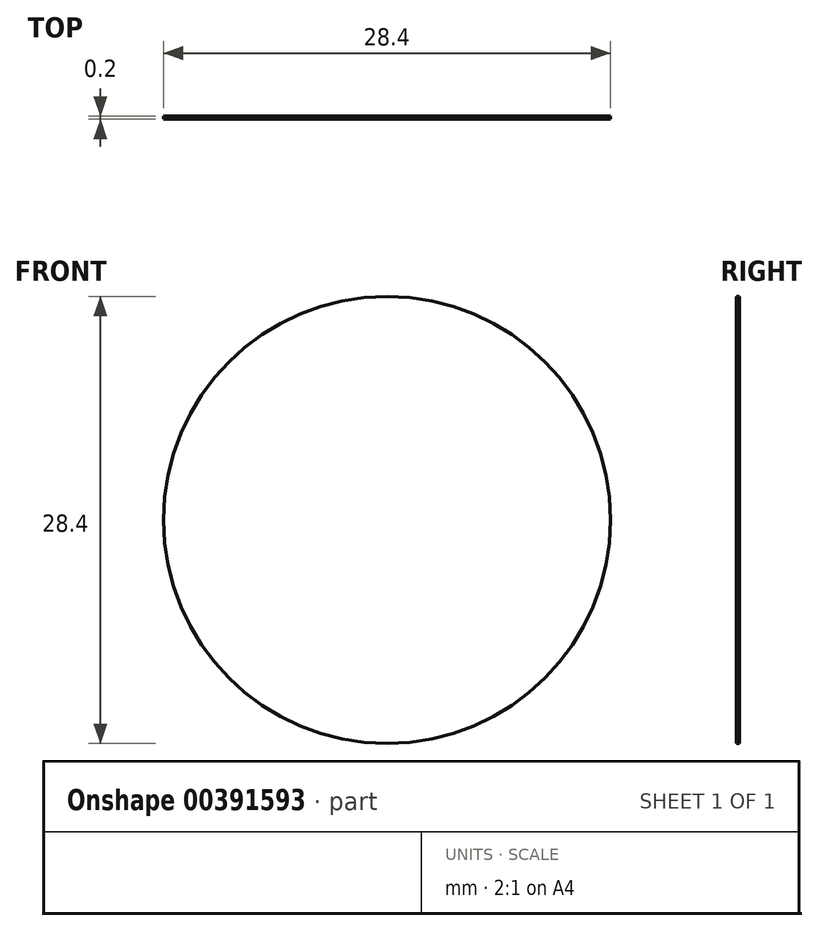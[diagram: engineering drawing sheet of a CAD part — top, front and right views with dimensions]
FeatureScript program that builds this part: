
annotation { "Feature Type Name" : "Feature", "Feature Type Description" : "" }
export const myFeature = defineFeature(function(context is Context, id is Id, definition is map)
    precondition{}
    {
        {
            var Q0;
            Q0=qCreatedBy(makeId("Front.planeOp"),FACE);
            var sketch = newSketch(context, id + "F0", { "sketchPlane" : qUnion([Q0])});
            skCircle(sketch, "E0", {"center": v(0, 0) * mm, "radius": 7 * mm, "construction": true});
            skCircle(sketch, "E1", {"center": v(0, 0) * mm, "radius": 10.5 * mm, "construction": true});
            skLineSegment(sketch, "E2", {"start": v(0, 7) * mm, "end": v(0.75, 7) * mm, "construction": true});
            skLineSegment(sketch, "E3", {"start": v(0.75, 7) * mm, "end": v(0.75, 13.5) * mm, "construction": true});
            skLineSegment(sketch, "E4", {"start": v(0.75, 13.5) * mm, "end": v(0, 13.5) * mm, "construction": true});
            skLineSegment(sketch, "E5", {"start": v(0, 13.5) * mm, "end": v(-0.75, 13.5) * mm, "construction": true});
            skLineSegment(sketch, "E6", {"start": v(-0.75, 13.5) * mm, "end": v(-0.75, 7) * mm, "construction": true});
            skLineSegment(sketch, "E7", {"start": v(-0.75, 7) * mm, "end": v(0, 7) * mm, "construction": true});
            skLineSegment(sketch, "E8.1.0", {"start": v(-2.85, 6.44) * mm, "end": v(-6.1, 12.07) * mm});
            skLineSegment(sketch, "E8.1.1", {"start": v(-7.4, 11.32) * mm, "end": v(-4.15, 5.69) * mm});
            skLineSegment(sketch, "E8.1.2", {"start": v(-4.15, 5.69) * mm, "end": v(-3.5, 6.06) * mm});
            skLineSegment(sketch, "E8.1.3", {"start": v(-3.5, 6.06) * mm, "end": v(-2.85, 6.44) * mm});
            skLineSegment(sketch, "E8.1.4", {"start": v(-6.1, 12.07) * mm, "end": v(-6.75, 11.7) * mm});
            skLineSegment(sketch, "E8.1.5", {"start": v(-6.75, 11.7) * mm, "end": v(-7.4, 11.32) * mm});
            skLineSegment(sketch, "E8.2.0", {"start": v(-5.69, 4.15) * mm, "end": v(-11.32, 7.4) * mm});
            skLineSegment(sketch, "E8.2.1", {"start": v(-12.07, 6.1) * mm, "end": v(-6.44, 2.85) * mm});
            skLineSegment(sketch, "E8.2.2", {"start": v(-6.44, 2.85) * mm, "end": v(-6.06, 3.5) * mm});
            skLineSegment(sketch, "E8.2.3", {"start": v(-6.06, 3.5) * mm, "end": v(-5.69, 4.15) * mm});
            skLineSegment(sketch, "E8.2.4", {"start": v(-11.32, 7.4) * mm, "end": v(-11.7, 6.75) * mm});
            skLineSegment(sketch, "E8.2.5", {"start": v(-11.7, 6.75) * mm, "end": v(-12.07, 6.1) * mm});
            skLineSegment(sketch, "E8.3.0", {"start": v(-7, 0.75) * mm, "end": v(-13.5, 0.75) * mm, "construction": true});
            skLineSegment(sketch, "E8.3.1", {"start": v(-13.5, -0.75) * mm, "end": v(-7, -0.75) * mm, "construction": true});
            skLineSegment(sketch, "E8.3.2", {"start": v(-7, -0.75) * mm, "end": v(-7, 0) * mm, "construction": true});
            skLineSegment(sketch, "E8.3.3", {"start": v(-7, 0) * mm, "end": v(-7, 0.75) * mm, "construction": true});
            skLineSegment(sketch, "E8.3.4", {"start": v(-13.5, 0.75) * mm, "end": v(-13.5, 0) * mm, "construction": true});
            skLineSegment(sketch, "E8.3.5", {"start": v(-13.5, 0) * mm, "end": v(-13.5, -0.75) * mm, "construction": true});
            skLineSegment(sketch, "E8.4.0", {"start": v(-6.44, -2.85) * mm, "end": v(-12.07, -6.1) * mm});
            skLineSegment(sketch, "E8.4.1", {"start": v(-11.32, -7.4) * mm, "end": v(-5.69, -4.15) * mm});
            skLineSegment(sketch, "E8.4.2", {"start": v(-5.69, -4.15) * mm, "end": v(-6.06, -3.5) * mm});
            skLineSegment(sketch, "E8.4.3", {"start": v(-6.06, -3.5) * mm, "end": v(-6.44, -2.85) * mm});
            skLineSegment(sketch, "E8.4.4", {"start": v(-12.07, -6.1) * mm, "end": v(-11.7, -6.75) * mm});
            skLineSegment(sketch, "E8.4.5", {"start": v(-11.7, -6.75) * mm, "end": v(-11.32, -7.4) * mm});
            skLineSegment(sketch, "E8.5.0", {"start": v(-4.15, -5.69) * mm, "end": v(-7.4, -11.32) * mm});
            skLineSegment(sketch, "E8.5.1", {"start": v(-6.1, -12.07) * mm, "end": v(-2.85, -6.44) * mm});
            skLineSegment(sketch, "E8.5.2", {"start": v(-2.85, -6.44) * mm, "end": v(-3.5, -6.06) * mm});
            skLineSegment(sketch, "E8.5.3", {"start": v(-3.5, -6.06) * mm, "end": v(-4.15, -5.69) * mm});
            skLineSegment(sketch, "E8.5.4", {"start": v(-7.4, -11.32) * mm, "end": v(-6.75, -11.7) * mm});
            skLineSegment(sketch, "E8.5.5", {"start": v(-6.75, -11.7) * mm, "end": v(-6.1, -12.07) * mm});
            skLineSegment(sketch, "E8.6.0", {"start": v(-0.75, -7) * mm, "end": v(-0.75, -13.5) * mm, "construction": true});
            skLineSegment(sketch, "E8.6.1", {"start": v(0.75, -13.5) * mm, "end": v(0.75, -7) * mm, "construction": true});
            skLineSegment(sketch, "E8.6.2", {"start": v(0.75, -7) * mm, "end": v(0, -7) * mm, "construction": true});
            skLineSegment(sketch, "E8.6.3", {"start": v(0, -7) * mm, "end": v(-0.75, -7) * mm, "construction": true});
            skLineSegment(sketch, "E8.6.4", {"start": v(-0.75, -13.5) * mm, "end": v(0, -13.5) * mm, "construction": true});
            skLineSegment(sketch, "E8.6.5", {"start": v(0, -13.5) * mm, "end": v(0.75, -13.5) * mm, "construction": true});
            skLineSegment(sketch, "E8.7.0", {"start": v(2.85, -6.44) * mm, "end": v(6.1, -12.07) * mm});
            skLineSegment(sketch, "E8.7.1", {"start": v(7.4, -11.32) * mm, "end": v(4.15, -5.69) * mm});
            skLineSegment(sketch, "E8.7.2", {"start": v(4.15, -5.69) * mm, "end": v(3.5, -6.06) * mm});
            skLineSegment(sketch, "E8.7.3", {"start": v(3.5, -6.06) * mm, "end": v(2.85, -6.44) * mm});
            skLineSegment(sketch, "E8.7.4", {"start": v(6.1, -12.07) * mm, "end": v(6.75, -11.7) * mm});
            skLineSegment(sketch, "E8.7.5", {"start": v(6.75, -11.7) * mm, "end": v(7.4, -11.32) * mm});
            skLineSegment(sketch, "E8.8.0", {"start": v(5.69, -4.15) * mm, "end": v(11.32, -7.4) * mm});
            skLineSegment(sketch, "E8.8.1", {"start": v(12.07, -6.1) * mm, "end": v(6.44, -2.85) * mm});
            skLineSegment(sketch, "E8.8.2", {"start": v(6.44, -2.85) * mm, "end": v(6.06, -3.5) * mm});
            skLineSegment(sketch, "E8.8.3", {"start": v(6.06, -3.5) * mm, "end": v(5.69, -4.15) * mm});
            skLineSegment(sketch, "E8.8.4", {"start": v(11.32, -7.4) * mm, "end": v(11.7, -6.75) * mm});
            skLineSegment(sketch, "E8.8.5", {"start": v(11.7, -6.75) * mm, "end": v(12.07, -6.1) * mm});
            skLineSegment(sketch, "E8.9.0", {"start": v(7, -0.75) * mm, "end": v(13.5, -0.75) * mm, "construction": true});
            skLineSegment(sketch, "E8.9.1", {"start": v(13.5, 0.75) * mm, "end": v(7, 0.75) * mm, "construction": true});
            skLineSegment(sketch, "E8.9.2", {"start": v(7, 0.75) * mm, "end": v(7, 0) * mm, "construction": true});
            skLineSegment(sketch, "E8.9.3", {"start": v(7, 0) * mm, "end": v(7, -0.75) * mm, "construction": true});
            skLineSegment(sketch, "E8.9.4", {"start": v(13.5, -0.75) * mm, "end": v(13.5, 0) * mm, "construction": true});
            skLineSegment(sketch, "E8.9.5", {"start": v(13.5, 0) * mm, "end": v(13.5, 0.75) * mm, "construction": true});
            skLineSegment(sketch, "E8.10.0", {"start": v(6.44, 2.85) * mm, "end": v(12.07, 6.1) * mm});
            skLineSegment(sketch, "E8.10.1", {"start": v(11.32, 7.4) * mm, "end": v(5.69, 4.15) * mm});
            skLineSegment(sketch, "E8.10.2", {"start": v(5.69, 4.15) * mm, "end": v(6.06, 3.5) * mm});
            skLineSegment(sketch, "E8.10.3", {"start": v(6.06, 3.5) * mm, "end": v(6.44, 2.85) * mm});
            skLineSegment(sketch, "E8.10.4", {"start": v(12.07, 6.1) * mm, "end": v(11.7, 6.75) * mm});
            skLineSegment(sketch, "E8.10.5", {"start": v(11.7, 6.75) * mm, "end": v(11.32, 7.4) * mm});
            skLineSegment(sketch, "E8.11.0", {"start": v(4.15, 5.69) * mm, "end": v(7.4, 11.32) * mm});
            skLineSegment(sketch, "E8.11.1", {"start": v(6.1, 12.07) * mm, "end": v(2.85, 6.44) * mm});
            skLineSegment(sketch, "E8.11.2", {"start": v(2.85, 6.44) * mm, "end": v(3.5, 6.06) * mm});
            skLineSegment(sketch, "E8.11.3", {"start": v(3.5, 6.06) * mm, "end": v(4.15, 5.69) * mm});
            skLineSegment(sketch, "E8.11.4", {"start": v(7.4, 11.32) * mm, "end": v(6.75, 11.7) * mm});
            skLineSegment(sketch, "E8.11.5", {"start": v(6.75, 11.7) * mm, "end": v(6.1, 12.07) * mm});
            skCircle(sketch, "E9", {"center": v(0, 0) * mm, "radius": 13.5 * mm, "construction": true});
            skSolve(sketch);
        }
        {
            var Q0;
            Q0=qCreatedBy(makeId("Front.planeOp"),FACE);
            var sketch = newSketch(context, id + "F1", { "sketchPlane" : qUnion([Q0])});
            skText(sketch, "E10", { "text": "12", "fontName": "AllertaStencil-Regular.ttf"});
            skText(sketch, "E11", { "text": "6", "fontName": "AllertaStencil-Regular.ttf"});
            skText(sketch, "E12", { "text": "9", "fontName": "AllertaStencil-Regular.ttf"});
            skPoint(sketch, "E13", {"position": v(-10.5, 0) * mm});
            skText(sketch, "E14", { "text": "3", "fontName": "AllertaStencil-Regular.ttf"});
            skCircle(sketch, "E15", {"center": v(0, 0) * mm, "radius": 10.5 * mm, "construction": true});
            skCircle(sketch, "E16", {"center": v(0, 0) * mm, "radius": 7 * mm, "construction": true});
            skLineSegment(sketch, "E17", {"start": v(0, 0) * mm, "end": v(0, 10.5) * mm, "construction": true});
            skLineSegment(sketch, "E18.1.0", {"start": v(0, 0) * mm, "end": v(-10.5, 0) * mm, "construction": true});
            skLineSegment(sketch, "E18.2.0", {"start": v(0, 0) * mm, "end": v(0, -10.5) * mm, "construction": true});
            skLineSegment(sketch, "E18.3.0", {"start": v(0, 0) * mm, "end": v(10.5, 0) * mm, "construction": true});
            skPoint(sketch, "E19", {"position": v(10.5, 0) * mm});
            const initialGuessF1  = {"E10": [-0.00246, 0.007, 1, 0, 0.0035], "E11": [-0.00153, -0.0105, 1, 0, 0.0035], "E12": [-0.0105, -0.00175, 1, 0, 0.0035], "E14": [0.00776, -0.00175, 1, 0, 0.0035]};
            skSetInitialGuess(sketch, initialGuessF1);
            skSolve(sketch);
        }
        {
            var Q0;
            Q0=qCreatedBy(makeId("Front.planeOp"),FACE);
            var sketch = newSketch(context, id + "F2", { "sketchPlane" : qUnion([Q0])});
            skLineSegment(sketch, "E20", {"start": v(0, 10.42) * mm, "end": v(1.75, 13.46) * mm});
            skLineSegment(sketch, "E21", {"start": v(1.75, 13.46) * mm, "end": v(-1.75, 13.46) * mm});
            skLineSegment(sketch, "E22", {"start": v(-1.75, 13.46) * mm, "end": v(0, 10.42) * mm});
            skLineSegment(sketch, "E23", {"start": v(-11.89, 0) * mm, "end": v(-11.89, 1.75) * mm});
            skLineSegment(sketch, "E24", {"start": v(-11.89, 1.75) * mm, "end": v(-13.39, 1.75) * mm});
            skLineSegment(sketch, "E25", {"start": v(-13.39, 1.75) * mm, "end": v(-13.39, -1.75) * mm});
            skLineSegment(sketch, "E26", {"start": v(-13.39, -1.75) * mm, "end": v(-11.89, -1.75) * mm});
            skLineSegment(sketch, "E27", {"start": v(-11.89, -1.75) * mm, "end": v(-11.89, 0) * mm});
            skCircle(sketch, "E28", {"center": v(0, 0) * mm, "radius": 11.25 * mm, "construction": true});
            skLineSegment(sketch, "E29.1.0", {"start": v(-1.75, -11.89) * mm, "end": v(-1.75, -13.39) * mm});
            skLineSegment(sketch, "E29.1.1", {"start": v(-1.75, -13.39) * mm, "end": v(1.75, -13.39) * mm});
            skLineSegment(sketch, "E29.1.2", {"start": v(1.75, -13.39) * mm, "end": v(1.75, -11.89) * mm});
            skLineSegment(sketch, "E29.1.3", {"start": v(1.75, -11.89) * mm, "end": v(0, -11.89) * mm});
            skLineSegment(sketch, "E29.1.4", {"start": v(0, -11.89) * mm, "end": v(-1.75, -11.89) * mm});
            skLineSegment(sketch, "E29.2.0", {"start": v(11.89, -1.75) * mm, "end": v(13.39, -1.75) * mm});
            skLineSegment(sketch, "E29.2.1", {"start": v(13.39, -1.75) * mm, "end": v(13.39, 1.75) * mm});
            skLineSegment(sketch, "E29.2.2", {"start": v(13.39, 1.75) * mm, "end": v(11.89, 1.75) * mm});
            skLineSegment(sketch, "E29.2.3", {"start": v(11.89, 1.75) * mm, "end": v(11.89, 0) * mm});
            skLineSegment(sketch, "E29.2.4", {"start": v(11.89, 0) * mm, "end": v(11.89, -1.75) * mm});
            skLineSegment(sketch, "E29.anchor1", {"start": v(0, 0) * mm, "end": v(-11.89, 0) * mm, "construction": true});
            skLineSegment(sketch, "E29.anchor2", {"start": v(0, 0) * mm, "end": v(11.89, 0) * mm, "construction": true});
            skCircle(sketch, "E30", {"center": v(0, 0) * mm, "radius": 14.2 * mm, "construction": true});
            skCircle(sketch, "E31", {"center": v(0, 0) * mm, "radius": 13.5 * mm, "construction": true});
            skLineSegment(sketch, "E32", {"start": v(0, 13.5) * mm, "end": v(0, 11.25) * mm, "construction": true});
            skCircle(sketch, "E33", {"center": v(0, 12.38) * mm, "radius": 1.13 * mm, "construction": true});
            skCircle(sketch, "E34.1.0", {"center": v(-6.19, 10.72) * mm, "radius": 1.13 * mm, "construction": true});
            skCircle(sketch, "E34.2.0", {"center": v(-10.72, 6.19) * mm, "radius": 1.13 * mm, "construction": true});
            skCircle(sketch, "E34.3.0", {"center": v(-12.38, 0) * mm, "radius": 1.13 * mm, "construction": true});
            skCircle(sketch, "E34.4.0", {"center": v(-10.72, -6.19) * mm, "radius": 1.13 * mm, "construction": true});
            skCircle(sketch, "E34.5.0", {"center": v(-6.19, -10.72) * mm, "radius": 1.13 * mm, "construction": true});
            skCircle(sketch, "E34.6.0", {"center": v(0, -12.38) * mm, "radius": 1.13 * mm, "construction": true});
            skCircle(sketch, "E34.7.0", {"center": v(6.19, -10.72) * mm, "radius": 1.13 * mm, "construction": true});
            skCircle(sketch, "E34.8.0", {"center": v(10.72, -6.19) * mm, "radius": 1.13 * mm, "construction": true});
            skCircle(sketch, "E34.9.0", {"center": v(12.38, 0) * mm, "radius": 1.13 * mm, "construction": true});
            skCircle(sketch, "E34.10.0", {"center": v(10.72, 6.19) * mm, "radius": 1.13 * mm, "construction": true});
            skCircle(sketch, "E34.11.0", {"center": v(6.19, 10.72) * mm, "radius": 1.13 * mm, "construction": true});
            skSolve(sketch);
        }
        {
            var Q0;
            Q0=qCreatedBy(makeId("Front.planeOp"),FACE);
            var sketch = newSketch(context, id + "F3", { "sketchPlane" : qUnion([Q0])});
            skCircle(sketch, "E35", {"center": v(0, 0) * mm, "radius": 14.2 * mm});
            skSolve(sketch);
        }
        {
            var Q0;
            Q0=qSketchRegion(id+"F3",true);
            extrude(context, id + "F4", {"entities" : qUnion([Q0]), "depth" : 0.2 * mm});
        }
    });
